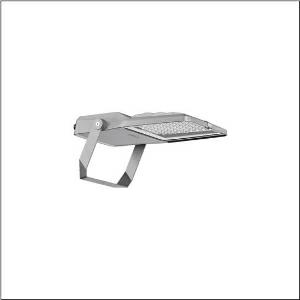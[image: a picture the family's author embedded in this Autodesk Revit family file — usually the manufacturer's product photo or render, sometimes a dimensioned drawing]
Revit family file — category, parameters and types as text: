
# Revit family: floodlight_fl_21_iq_mini___pl33t_5xa7772c1f1a_9de6
name_source: partatom
category: Lighting Fixtures
units: mm (PartAtom-declared; Revit-internal decimal feet)

## family parameters
Cut with Voids When Loaded = No
Host = Face
Light Source = No
Part Type = Normal
Room Calculation Point = No
Round Connector Dimension = Use Diameter
Shared = No

## types (1)
- --- (1 x LED, 10000 lm, 87.2 W, 2200K)
    Apparent Load = 87 VA
    CIE Flux Codes = 26 75 99 100 100
    Color Rendering = 70
    Color Temperature = 2200K
    Default Elevation = 1800 mm
    Description = Floodlight FL 21 iQ mini, floodlight, primary light control with lens, of PMMA, primary optical cover: protective disc, of toughened safety glass, transparent, light distribution: PL33T, light emission: direct distribution, installation type: surface-mounted, lamps: LED, High Power LED, rated values: 10.000lm | 87,2W | 114,7lm/W (begin service life); end service life: 10.000lm | 92,1W; at 50% lumin. flux: 5.000lm | 40,1W | 124,7lm/W, colour temperature: 2200K, colour rendering: CRI > 70, light colour: 722, light setting 1 begin service life: 100% | 10.000lm | 87,2W | 114,7lm/W | 2.200K, light setting 1 end service life: 92,1W, further light settings possible, control: Street-Remote, Auto-Match, Temp-Guard, Night-Set, Smart-Wire, Desk-Remote (wireless, voltage-free reading and setting of iQ features in the workshop via application-optimized NFC function/RFID function), optimised constant luminous flux control (CLO 2.0), pre-setting: linear dimming characteristic, with terminal, 6-pole, mains connection: 220..240V, AC, 50/60Hz, luminaire housing, of diecast aluminium, powder-coated, SITECO metallic grey (DB 702S), corrosivity category C5 mid according to DIN EN ISO 12944suitable for swimming poolschlorine-resistant, sealing non-destructively replaceable, mounting bracket, of steel, galvanised, powder-coated, SITECO metallic grey (DB 702S), protection rating (complete): IP66, insulation class (complete): insulation class II (safety insulation), certification: CE, ENEC, VDE, protection symbol: D, impact resistance: IK08, permissible operating ambient temperature: -40..+40°C, permissible operating ambient temperature for outdoor applications: -40..+50°C, standard: DIN EN 12944, LABS conformity tested according to VDMA 24364:2018-05, packaging unit: 1 piece

Light Distribution: PL33T
    Height = 70 mm
    Lamp = 1 x LED
    Lamp Light Flux = 10000 lm
    Lamp Power = 87.2 W
    Lamp count = 1
    Length = 485 mm
    Luminous efficacy = 115 lm/W
    Manufacturer = Siteco
    ModVariant = No
    Model = 5XA7772C1F1A
    Number of Poles = 1
    OnlyDefault = Yes
    Power Factor = 1
    Product Name = Floodlight FL 21 iQ mini | PL33T
    Product group = floodlight | pylon annexe
    ProductGroupID = 6201
    Protection Class = Protection class II
    Protection Degree = IP 66
    RLX_Detail_Level = 1
    RLX_Emergency_Light_Flux = 0 lm
    RLX_Emergency_Type = 0
    RLX_Emergency_Type_DB = No
    RlxData = <blob elided: 96217 chars, md5=01aab61d>
    Socket = socket
    Standby Power = 0 W
    System Light Flux = 10000 lm
    System Power = 87 W
    Type Comments = factory setting: luminous flux: 100 % | dim-lin: 254 | 456 mA
    Type Image = l_1006845.jpg
    URL = http://relux.com
    VarID = @adj_149095
    Voltage = 0 V
    Weight = 0.00 kg
    Width = 337 mm

## geometry (parser evidence)
native form markers: Blend x4, Sweep x12
no freeform markers — native parametric forms only
